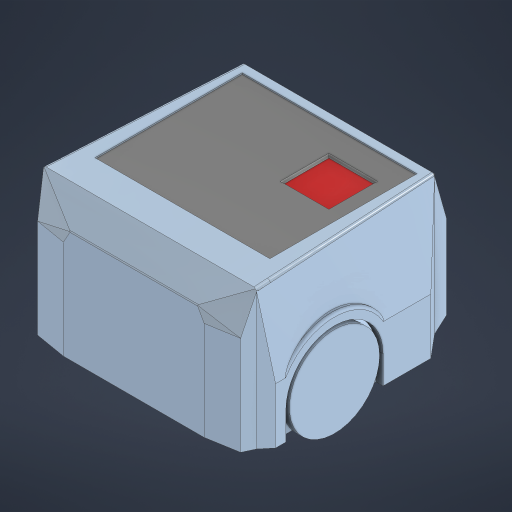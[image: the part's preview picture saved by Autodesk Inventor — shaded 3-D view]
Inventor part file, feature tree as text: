
AUTODESK INVENTOR PART (.ipt)
format: ipt  version: 2024 (Build 280153000, 153)  size: 2,027,520 bytes
history: native  units: mm
features: other x56, sketch x42, extrude x40, loft x18, fillet x8, plane x1
ambient origin geometry x8: Origin, YZ Plane, XZ Plane, XY Plane, X Axis, Y Axis, Z Axis, Center Point
bodies: Body1 (feature_tree), Body2 (feature_tree)
feature tree (165):
  other  "Sólido1"
  extrude  "Base"  Depth=10.0mm TaperAngle=0.0deg
  extrude  "Llantas"  Depth=70.0mm
  extrude  "Carroceria"  Depth=75.0mm
  extrude  "Extrusión30"  Depth=150.0mm
  extrude  "Extrusión31"  Depth=10.0mm TaperAngle=0.0deg
  extrude  "Extrusión32"  Depth=8.726646mm
  extrude  "Extrusión33"  Depth=40.0mm
  extrude  "Extrusión34"  Depth=15.0mm
  extrude  "Extrusión35"  Depth=50.0mm
  extrude  "Extrusión38"  Depth=11.34464mm
  extrude  "Extrusión39"  Depth=5.0mm
  extrude  "Extrusión100"  Depth=3.0mm
  extrude  "Extrusión102"  Depth=5.0mm
  extrude  "Extrusión103"  Depth=3.0mm
  extrude  "Extrusión104"  TaperAngle=0.0deg  [1 undecoded]
  loft  "Solevación32"
  loft  "Solevación33"
  extrude  "Extrusión43"  TaperAngle=0.0deg  [1 undecoded]
  extrude  "Extrusión96"  Depth=3.0mm
  extrude  "Extrusión110"  Depth=3.0mm
  extrude  "Extrusión90"  Depth=3.0mm
  extrude  "Extrusión94"  Depth=3.0mm
  extrude  "Extrusión95"  Depth=3.0mm
  loft  "Solevación10"
  loft  "Solevación11"
  extrude  "Extrusión53"  TaperAngle=0.0deg  [1 undecoded]
  extrude  "Extrusión93"  TaperAngle=0.0deg  [1 undecoded]
  loft  "Solevación8"
  loft  "Solevación9"
  extrude  "Extrusión84"  Depth=80.0mm TaperAngle=0.0deg
  extrude  "Extrusión64"  Depth=5.0mm
  extrude  "Extrusión65"  Depth=5.0mm TaperAngle=0.0deg
  extrude  "Extrusión67"  Depth=5.0mm TaperAngle=0.0deg
  extrude  "Extrusión111"  Depth=6.0mm
  plane  "Plano de trabajo5"
  extrude  "Extrusión98"  Depth=3.0mm
  loft  "Solevación18"
  loft  "Solevación19"
  loft  "Solevación20"
  loft  "Solevación21"
  loft  "Solevación22"
  loft  "Solevación23"
  loft  "Solevación24"
  loft  "Solevación30"
  loft  "Solevación26"
  loft  "Solevación31"
  loft  "Solevación34"
  loft  "Solevación35"
  fillet  "Empalme1"  Radius=100.0mm
  fillet  "Empalme2"  [1 undecoded]
  fillet  "Empalme3"  Radius=30.0mm
  fillet  "Empalme4"  Radius=10.0mm
  fillet  "Empalme5"  Radius=11.34464mm
  fillet  "Empalme6"  Radius=10.0mm
  fillet  "Empalme7"  Radius=11.34464mm
  extrude  "Extrusión105"  TaperAngle=0.0deg  [1 undecoded]
  extrude  "Extrusión106"  Depth=10.0mm TaperAngle=0.0deg
  extrude  "Extrusión107"  Depth=12.0mm
  extrude  "Extrusión108"  Depth=10.0mm
  extrude  "Extrusión109"  Depth=12.0mm TaperAngle=0.0deg
  extrude  "Extrusión112"  TaperAngle=0.0deg  [1 undecoded]
  extrude  "Extrusión113"  Depth=12.0mm
  extrude  "Extrusión114"  Depth=12.0mm
  extrude  "Extrusión115"  Depth=12.0mm
  extrude  "Extrusión116"  Depth=12.0mm
  extrude  "Extrusión117"  Depth=12.0mm TaperAngle=0.0deg
  fillet  "Empalme8"  Radius=5.0mm
  sketch  "Boceto Base"  dims[d424=37.5mm d425=5.0mm]
  sketch  "Boceto Llantas"  dims[d426=5.0mm d427=5.0mm]
  sketch  "Boceto Carroceria"  dims[d428=5.0mm d429=15.0mm d430=0.0mm d431=10.0mm d432=5.0mm d433=85.592mm d434=0.0mm d439=10.0mm d440=0.0mm d494=10.0mm d495=0.0mm d514=100.0mm d515=0.0mm d530=30.0deg d531=30.0mm d532=10.0mm d533=0.0mm d534=0.0mm d535=90.0deg d536=0.0mm d537=90.0deg d538=0.0mm d539=90.0deg d540=0.0mm d541=90.0deg d542=11.34464mm d543=10.0mm d544=0.0mm d545=11.34464mm d546=0.0mm d547=10.0mm d548=0.0mm d549=5.0mm d550=10.0mm d551=105.0mm d552=0.0mm d553=0.0mm d554=90.0deg d559=0.0mm d560=90.0deg d595=20.0mm d596=20.0mm d597=30.0mm d598=30.0mm d599=5.0mm d600=0.0mm d611=5.0mm d612=0.0mm d613=90.0deg d614=0.0mm d615=90.0deg d616=0.0mm d617=90.0deg d618=0.0mm d619=90.0deg d620=0.0mm d621=90.0deg d622=0.0mm d623=90.0deg d624=0.0mm d625=90.0deg d626=0.0mm d627=90.0deg d628=0.0mm d629=90.0deg d630=0.0mm d631=90.0deg d632=5.0mm d633=0.0mm d634=90.0deg d635=0.0mm d636=90.0deg d637=0.0mm d638=90.0deg d639=0.0mm d640=90.0deg d645=0.0mm d646=90.0deg d647=0.0mm d648=90.0deg d653=20.0mm d654=85.0mm d655=42.5mm d656=70.0mm d657=200.0mm d658=0.0mm d669=40.0mm d670=0.0mm d671=0.0mm d672=90.0deg d673=0.0mm d674=90.0deg d676=0.0mm d677=90.0deg d680=0.0mm d681=90.0deg d684=5.0mm d685=0.0mm d686=5.0mm d687=0.0mm d688=0.0mm d689=90.0deg d690=0.0mm d691=90.0deg d692=0.0mm d693=90.0deg d694=0.0mm d695=90.0deg d697=0.0mm d698=90.0deg d699=0.0mm d700=90.0deg d701=0.0mm d702=90.0deg d703=0.0mm d704=90.0deg d705=2.0mm d706=2.0mm d707=2.0mm d708=2.0mm d709=2.0mm d710=2.0mm d711=2.0mm d712=100.0mm d713=0.0mm d714=100.0mm d715=0.0mm d716=10.0mm d717=15.0mm d718=10.0mm d719=10.0mm d720=15.0mm d723=10.0mm d724=10.0mm d725=3.0mm d726=5.0mm d727=5.0mm d728=3.0mm d729=5.0mm d730=5.0mm d731=5.0mm d732=0.0mm d733=5.0mm d734=10.0mm d735=0.0mm d737=5.0mm d738=10.0mm d739=0.0mm d740=3.0mm d741=120.0deg d742=120.0deg d743=3.0mm d744=120.0deg d745=3.0mm d746=120.0deg d747=2.598mm d748=5.196152mm d749=3.0mm d750=2.0mm d751=0.0mm d752=3.0mm d753=3.0mm d754=120.0deg d755=3.0mm d756=120.0deg d757=3.0mm d758=3.0mm d759=120.0deg d760=3.0mm d761=2.598mm d762=2.0mm d763=0.0mm d764=0.0mm d765=90.0deg d766=0.0mm d767=90.0deg d768=10.0mm d769=0.0mm d770=1.0mm d771=0.0mm d772=10.5mm d774=35.0mm d778=3.0mm d779=0.0mm d783=65.0mm d784=0.0mm d785=5.0mm d786=0.0mm d787=0.0mm d788=35.0mm d789=65.0mm d790=5.0mm d791=0.0mm d792=30.0mm d793=12.5mm d794=0.0mm d795=12.0mm d796=18.0mm d797=35.0mm d64=0.5mm d65=0.872665mm d66=0.5mm d67=0.872665mm d229=0.5mm d230=0.872665mm d231=0.5mm d232=0.872665mm d284=0.5mm d285=0.872665mm d286=0.5mm d287=0.872665mm d288=0.5mm d289=0.872665mm d290=0.5mm d342=0.5mm d343=0.872665mm d344=0.5mm d345=0.872665mm d352=0.5mm d353=0.872665mm d354=0.5mm d355=0.872665mm d364=0.5mm d365=0.872665mm d366=0.5mm d367=0.872665mm d386=0.5mm d387=0.872665mm d388=0.5mm d389=0.872665mm d472=0.5mm d473=0.872665mm d474=0.5mm d475=0.872665mm d525=0.5mm d526=0.872665mm d527=0.5mm d528=0.872665mm]
  sketch  "Boceto28"  dims[d0=160.0mm d2=10.0mm d3=0.0mm]
  sketch  "Boceto30"  dims[d4=70.0mm d5=70.0mm]
  sketch  "Boceto31"  dims[d6=20.0mm d7=75.0mm]
  sketch  "Boceto32"  dims[d8=80.0mm d9=150.0mm]
  sketch  "Boceto33"  dims[d10=25.0mm d11=10.0mm d12=0.0mm]
  sketch  "Boceto34"  dims[d13=30.0mm d14=8.726646mm]
  sketch  "Boceto37"  dims[d15=11.34464mm d16=40.0mm]
  sketch  "Boceto38"  dims[d17=15.0mm d18=15.0mm]
  sketch  "Boceto43"  dims[d19=6.0mm d20=50.0mm]
  sketch  "Boceto54"  dims[d21=8.726646mm d22=11.34464mm]
  sketch  "Boceto64"  dims[d23=6.0mm d24=5.0mm]
  sketch  "Boceto65"  dims[d25=10.0mm d26=0.0mm d291=3.0mm]
  sketch  "Boceto67"  dims[d292=5.0mm d293=5.0mm]
  sketch  "Boceto106"  dims[d294=3.0mm d295=5.0mm]
  sketch  "Boceto114"  dims[d297=3.0mm d298=0.0mm]
  sketch  "Boceto117"  dims[d299=0.0mm d300=0.0mm]
  sketch  "Boceto118"  dims[d301=0.0mm d303=5.0mm]
  sketch  "Boceto119"  dims[d304=3.0mm d305=0.0mm]
  sketch  "Boceto120"  dims[d306=5.0mm d307=3.0mm]
  sketch  "Boceto125"  dims[d308=5.0mm d309=3.0mm]
  sketch  "Boceto129"  dims[d310=5.0mm d311=3.0mm]
  other  "Aristas31"
  other  "Aristas32"
  other  "Aristas33"
  other  "Aristas34"
  other  "Aristas35"
  other  "Aristas36"
  other  "Aristas37"
  other  "Aristas38"
  other  "Aristas39"
  sketch  "Boceto131"  dims[d312=5.0mm d313=3.0mm]
  other  "Aristas40"
  other  "Aristas47"
  other  "Aristas48"
  other  "Sólido8"
  other  "Aristas49"
  other  "Aristas50"
  sketch  "Boceto132"  dims[d314=3.0mm d315=5.0mm]
  sketch  "Boceto135"  dims[d316=0.0mm d317=0.0mm]
  other  "Aristas57"
  other  "Aristas58"
  other  "Aristas59"
  other  "Aristas60"
  sketch  "Boceto138"  dims[d318=0.0mm d319=0.0mm]
  sketch  "Boceto139"  dims[d320=0.0mm d321=0.0mm]
  other  "Aristas65"
  other  "Aristas66"
  other  "Aristas67"
  other  "Aristas68"
  other  "Aristas69"
  other  "Aristas70"
  other  "Aristas71"
  other  "Aristas72"
  sketch  "Boceto142"  dims[d322=0.0mm d323=0.0mm]
  sketch  "Boceto143"  dims[d324=0.0mm d325=0.0mm]
  sketch  "Boceto144"  dims[d326=0.0mm d327=0.1mm d328=0.0mm]
  sketch  "Boceto145"  dims[d329=0.0mm d330=80.0mm d331=0.0mm]
  sketch  "Boceto146"  dims[d332=71.0mm d333=0.0mm d334=5.0mm]
  sketch  "Boceto148"  dims[d335=5.0mm d336=5.0mm d337=0.0mm]
  other  "Aristas73"
  other  "Aristas74"
  other  "Aristas75"
  other  "Aristas76"
  sketch  "Boceto149"  dims[d338=100.0mm d339=0.0mm d340=5.0mm d341=0.0mm]
  other  "Aristas77"
  other  "Aristas78"
  other  "Aristas79"
  other  "Aristas80"
  sketch  "Boceto150"  dims[d346=5.0mm d347=0.0mm d348=6.0mm]
  sketch  "Boceto152"  dims[d349=70.0mm d350=0.0mm d368=3.0mm]
  sketch  "Boceto153"  dims[d369=5.0mm d370=47.5mm]
  sketch  "Boceto154"  dims[d371=5.0mm d372=5.0mm]
  sketch  "Boceto155"  dims[d373=5.0mm d374=15.0mm d375=0.0mm]
  sketch  "Boceto156"  dims[d396=70.0mm d397=0.0mm d422=3.0mm]
  other  "Finish1"
  other  "Finish2"
  other  "Finish3"
  other  "Finish4"
  other  "Finish5"
  other  "Finish6"
  other  "Finish7"
  other  "Finish8"
  other  "Finish9"
  other  "Finish10"
  other  "Finish11"
  other  "Finish12"
  other  "Finish13"
  other  "Finish14"
  other  "Finish15"
  other  "Finish16"
  other  "Finish17"
  other  "Finish18"
  other  "Finish19"
  other  "Finish20"
note: 7 required parameter values undecoded (feature->parameter linkage not recoverable at this tier; creation-order binding heuristic only, values carry confidence <= 0.55)
